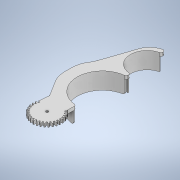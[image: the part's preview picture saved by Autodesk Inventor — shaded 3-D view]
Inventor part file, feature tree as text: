
AUTODESK INVENTOR PART (.ipt)
format: ipt  version: 2021 (Build 250183000, 183)  size: 582,656 bytes
history: native  units: mm
features: sketch x13, extrude x12, fillet x6
ambient origin geometry x8: Origin, YZ Plane, XZ Plane, XY Plane, X Axis, Y Axis, Z Axis, Center Point
bodies: Solid1 (feature_tree)
feature tree (31):
  extrude  "Extrusion1"  Depth=30.0mm
  extrude  "Extrusion4"  Depth=0.5mm
  extrude  "Extrusion6"  Depth=310.0mm TaperAngle=360.0deg
  extrude  "Extrusion9"  Depth=30.0mm
  extrude  "Extrusion10"  Depth=4.0mm TaperAngle=0.0deg
  extrude  "Extrusion11"  Depth=2.0mm
  fillet  "Fillet4"  Radius=2.0mm
  sketch  "Sketch14"  dims[d49=40.0mm d50=20.0mm d51=0.0mm]
  extrude  "Extrusion12"  Depth=10.0mm TaperAngle=0.0deg
  fillet  "Fillet5"  Radius=3.0mm
  fillet  "Fillet6"  Radius=10.0mm
  fillet  "Fillet7"  Radius=40.0mm
  fillet  "Fillet8"  Radius=10.0mm
  extrude  "Extrusion13"  Depth=20.0mm
  fillet  "Fillet9"  Radius=5.0mm
  extrude  "Extrusion14"  Depth=4.0mm TaperAngle=0.0deg
  extrude  "Extrusion5"  Depth=20.0mm TaperAngle=0.0deg
  extrude  "Extrusion2"  Depth=4.0mm TaperAngle=0.0deg
  extrude  "Extrusion3"  Depth=30.0mm
  sketch  "Sketch1"  dims[d0=30.0mm d1=35.0mm]
  sketch  "Sketch2"  dims[d2=0.5mm d4=0.5mm]
  sketch  "Sketch3"  dims[d6=0.1mm d7=310.0mm d9=360.0deg]
  sketch  "Sketch4"  dims[d13=60.0mm d14=30.0mm]
  sketch  "Sketch5"  dims[d15=10.0mm d19=4.0mm d20=0.0mm]
  sketch  "Sketch6"  dims[d22=10.0mm d23=0.1mm d24=2.0mm]
  sketch  "Sketch10"  dims[d25=3.0mm d26=0.0mm d27=3.0mm d28=0.0mm d29=3.0mm d30=10.0mm d31=0.0mm d32=40.0mm d33=10.0mm d34=0.0mm]
  sketch  "Sketch12"  dims[d35=20.0mm d36=0.0mm d43=22.0mm d44=5.0mm d45=0.0mm]
  sketch  "Sketch13"  dims[d46=40.0mm d47=4.0mm d48=0.0mm]
  sketch  "Sketch15"  dims[d52=21.0mm d53=4.0mm d54=0.0mm]
  sketch  "Sketch16"  dims[d55=1614.0mm d56=30.0mm]
  sketch  "Sketch17"  dims[d57=2.0mm d58=2.0mm d59=4.0mm d60=0.0mm d61=2.25mm d62=20.0mm d63=0.0mm d11=0.5mm d12=0.872665mm d64=0.5mm d65=0.872665mm d66=0.5mm d67=0.872665mm]
